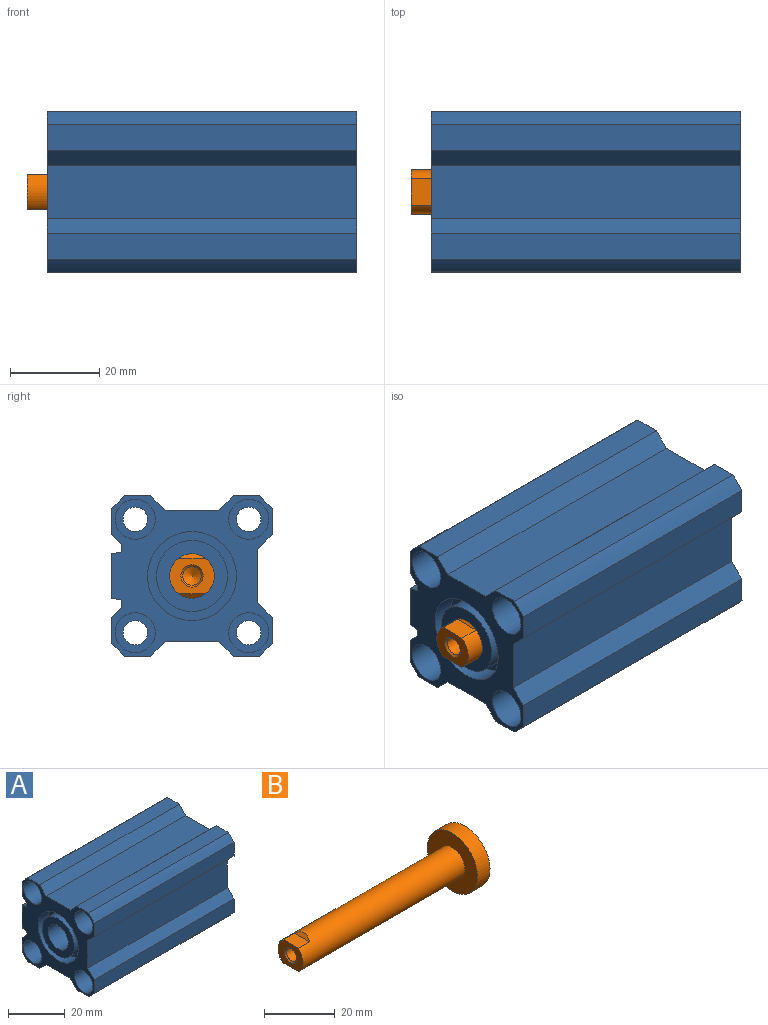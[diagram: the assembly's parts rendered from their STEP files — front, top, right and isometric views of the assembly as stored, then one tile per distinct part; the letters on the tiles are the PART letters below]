
ASSEMBLY  parts=2 mates=1
PART A: 66 faces, bbox 69.5x36x36 mm
  f0: plane 20x20mm, normal (-1,0,0), area 314.2mm2, adj f1
  f1: cylinder r=10mm len=55mm, axis (1,0,0), area 3455.8mm2, adj f0,f2
  f2: plane 20x20mm, normal (1,0,0), area 235.6mm2, adj f1,f3
  f3: cylinder r=5mm len=10mm, axis (1,0,0), area 314.2mm2, adj f2,f4
  f4: plane 16x16mm, normal (-1,0,0), area 122.5mm2, adj f3,f7
  f5: plane 4.13x4.13mm, normal (0,1,0), area 13.4mm2, adj f8
  f6: plane 4.13x4.13mm, normal (0,1,0), area 13.4mm2, adj f9
  f7: cylinder r=8mm len=16mm, axis (-1,0,0), area 251.3mm2, adj f4,f18
  f8: cylinder r=2.07mm len=5.57mm, axis (0,-1,0), area 72.3mm2, adj f5,f19
  f9: cylinder r=2.07mm len=5.57mm, axis (0,-1,0), area 72.3mm2, adj f6,f20
  f10: cylinder r=2.75mm len=55.5mm, axis (1,0,0), area 959mm2, adj f14,f21
  f11: cylinder r=2.75mm len=55.5mm, axis (1,0,0), area 959mm2, adj f15,f22
  f12: cylinder r=2.75mm len=55.5mm, axis (1,0,0), area 959mm2, adj f16,f23
  f13: cylinder r=2.75mm len=55.5mm, axis (1,0,0), area 959mm2, adj f17,f24
  f14: plane 9x9mm, normal (-1,0,0), area 39.9mm2, adj f10,f26
  f15: plane 9x9mm, normal (-1,0,0), area 39.9mm2, adj f11,f27
  f16: plane 9x9mm, normal (-1,0,0), area 39.9mm2, adj f12,f28
  f17: plane 9x9mm, normal (-1,0,0), area 39.9mm2, adj f13,f29
  f18: plane 20x20mm, normal (-1,0,0), area 113.1mm2, adj f7,f30
  f19: cone r=0mm half-angle=45deg, axis (0,1,0), area 8.8mm2, adj f8,f51
  f20: cone r=0mm half-angle=45deg, axis (0,1,0), area 8.8mm2, adj f9,f51
  f21: plane 9x9mm, normal (1,0,0), area 39.9mm2, adj f10,f55
  f22: plane 9x9mm, normal (1,0,0), area 39.9mm2, adj f11,f56
  f23: plane 9x9mm, normal (1,0,0), area 39.9mm2, adj f12,f57
  f24: plane 9x9mm, normal (1,0,0), area 39.9mm2, adj f13,f58
  f25: plane 20x20mm, normal (1,0,0), area 314.2mm2, adj f59
  f26: cylinder r=4.5mm len=9mm, axis (1,0,0), area 197.9mm2, adj f14,f61
  f27: cylinder r=4.5mm len=9mm, axis (1,0,0), area 197.9mm2, adj f15,f61
  f28: cylinder r=4.5mm len=9mm, axis (1,0,0), area 197.9mm2, adj f16,f61
  f29: cylinder r=4.5mm len=9mm, axis (1,0,0), area 197.9mm2, adj f17,f61
  f30: cylinder r=10mm len=20mm, axis (-1,0,0), area 314.2mm2, adj f18,f61
  f31: plane 69.5x12mm, normal (0,0,1), area 834mm2, adj f32,f61,f62,f63
  f32: plane 69.5x3.25mm, normal (0,0.71,0.71), area 319.4mm2, adj f31,f33,f61,f63
  f33: plane 69.5x5.86mm, normal (0,0,1), area 407.1mm2, adj f32,f34,f61,f63
  f34: cylinder r=23.5mm len=69.5mm, axis (-1,0,0), area 284.6mm2, adj f33,f35,f61,f63
  f35: plane 69.5x5.86mm, normal (0,-1,0), area 407.1mm2, adj f34,f36,f61,f63
  f36: plane 69.5x3.25mm, normal (0,-0.71,-0.71), area 319.4mm2, adj f35,f37,f61,f63
  f37: plane 69.5x12mm, normal (0,-1,0), area 834mm2, adj f36,f38,f61,f63
  f38: plane 69.5x3.25mm, normal (0,-0.71,0.71), area 319.4mm2, adj f37,f39,f61,f63
  f39: plane 69.5x5.86mm, normal (0,-1,0), area 407.1mm2, adj f38,f40,f61,f63
  f40: cylinder r=23.5mm len=69.5mm, axis (-1,0,0), area 284.6mm2, adj f39,f41,f61,f63
  f41: plane 69.5x5.86mm, normal (0,0,-1), area 407.1mm2, adj f40,f42,f61,f63
  f42: plane 69.5x3.25mm, normal (0,0.71,-0.71), area 319.4mm2, adj f41,f43,f61,f63
  f43: plane 69.5x12mm, normal (0,0,-1), area 834mm2, adj f42,f44,f61,f63
  f44: plane 69.5x3.25mm, normal (0,-0.71,-0.71), area 319.4mm2, adj f43,f45,f61,f63
  f45: plane 69.5x5.86mm, normal (0,0,-1), area 407.1mm2, adj f44,f46,f61,f63
  f46: cylinder r=23.5mm len=69.5mm, axis (-1,0,0), area 284.6mm2, adj f45,f47,f61,f63
  f47: plane 69.5x5.86mm, normal (0,1,0), area 407.1mm2, adj f46,f48,f61,f63
  f48: plane 69.5x2.25mm, normal (0,0.71,0.71), area 221.1mm2, adj f47,f49,f61,f63
  f49: plane 69.5x1.6mm, normal (0,1,0), area 111.4mm2, adj f48,f50,f61,f63
  f50: plane 69.5x2.25mm, normal (0,0.17,-0.98), area 158.8mm2, adj f49,f51,f61,f63
  f51: plane 69.5x10mm, normal (0,1,0), area 655.7mm2, adj f19,f20,f50,f52,f61,f63
  f52: plane 69.5x2.25mm, normal (0,0.17,0.98), area 158.8mm2, adj f51,f53,f61,f63
  f53: plane 69.5x1.6mm, normal (0,1,0), area 111.4mm2, adj f52,f54,f61,f63
  f54: plane 69.5x2.25mm, normal (0,0.71,-0.71), area 221.1mm2, adj f53,f60,f61,f63
  f55: cylinder r=4.5mm len=9mm, axis (1,0,0), area 197.9mm2, adj f21,f63
  f56: cylinder r=4.5mm len=9mm, axis (1,0,0), area 197.9mm2, adj f22,f63
  f57: cylinder r=4.5mm len=9mm, axis (1,0,0), area 197.9mm2, adj f23,f63
  f58: cylinder r=4.5mm len=9mm, axis (1,0,0), area 197.9mm2, adj f24,f63
  f59: cylinder r=10mm len=20mm, axis (1,0,0), area 125.7mm2, adj f25,f63
  f60: plane 69.5x5.86mm, normal (0,1,0), area 407.1mm2, adj f54,f61,f63,f64
  f61: plane 36x36mm, normal (-1,0,0), area 549.8mm2, adj f26,f27,f28,f29,f30,f31,f32,f33
  f62: plane 69.5x3.25mm, normal (0,-0.71,0.71), area 319.4mm2, adj f31,f61,f63,f65
  f63: plane 36x36mm, normal (1,0,0), area 549.8mm2, adj f31,f32,f33,f34,f35,f36,f37,f38
  f64: cylinder r=23.5mm len=69.5mm, axis (-1,0,0), area 284.6mm2, adj f60,f61,f63,f65
  f65: plane 69.5x5.86mm, normal (0,0,1), area 407.1mm2, adj f61,f62,f63,f64
PART B: 12 faces, bbox 69.5x20x20 mm
  f0: plane 20x20mm, normal (1,0,0), area 314.2mm2, adj f1
  f1: cylinder r=10mm len=20mm, axis (1,0,0), area 314.2mm2, adj f0,f3
  f2: cone r=0mm half-angle=60deg, axis (-1,0,0), area 15.5mm2, adj f6
  f3: plane 20x20mm, normal (-1,0,0), area 235.6mm2, adj f1,f8
  f4: plane 6x1mm, normal (-0.71,0,-0.71), area 5.8mm2, adj f7,f8
  f5: plane 6x1mm, normal (-0.71,0,0.71), area 5.8mm2, adj f8,f9
  f6: cylinder r=2.07mm len=6.57mm, axis (1,0,0), area 85.3mm2, adj f2,f10
  f7: plane 6x4.5mm, normal (0,0,-1), area 27mm2, adj f4,f8,f11
  f8: cylinder r=5mm len=64.5mm, axis (1,0,0), area 1959.9mm2, adj f3,f4,f5,f7,f9,f11
  f9: plane 6x4.5mm, normal (0,0,1), area 27mm2, adj f5,f8,f11
  f10: cone r=0mm half-angle=45deg, axis (-1,0,0), area 8.8mm2, adj f6,f11
  f11: plane 10x8mm, normal (-1,0,0), area 50.7mm2, adj f7,f8,f9,f10
PLACE A t=(-18.73,-11.45,12.79)mm fixed
PLACE B rot(axis=(-1,0,0),0deg) t=(-18.73,-11.45,12.79)mm
MATE slider A.f1 <-> B.f1  axis (-1,0,0) through (46.27,-11.45,12.79)mm
